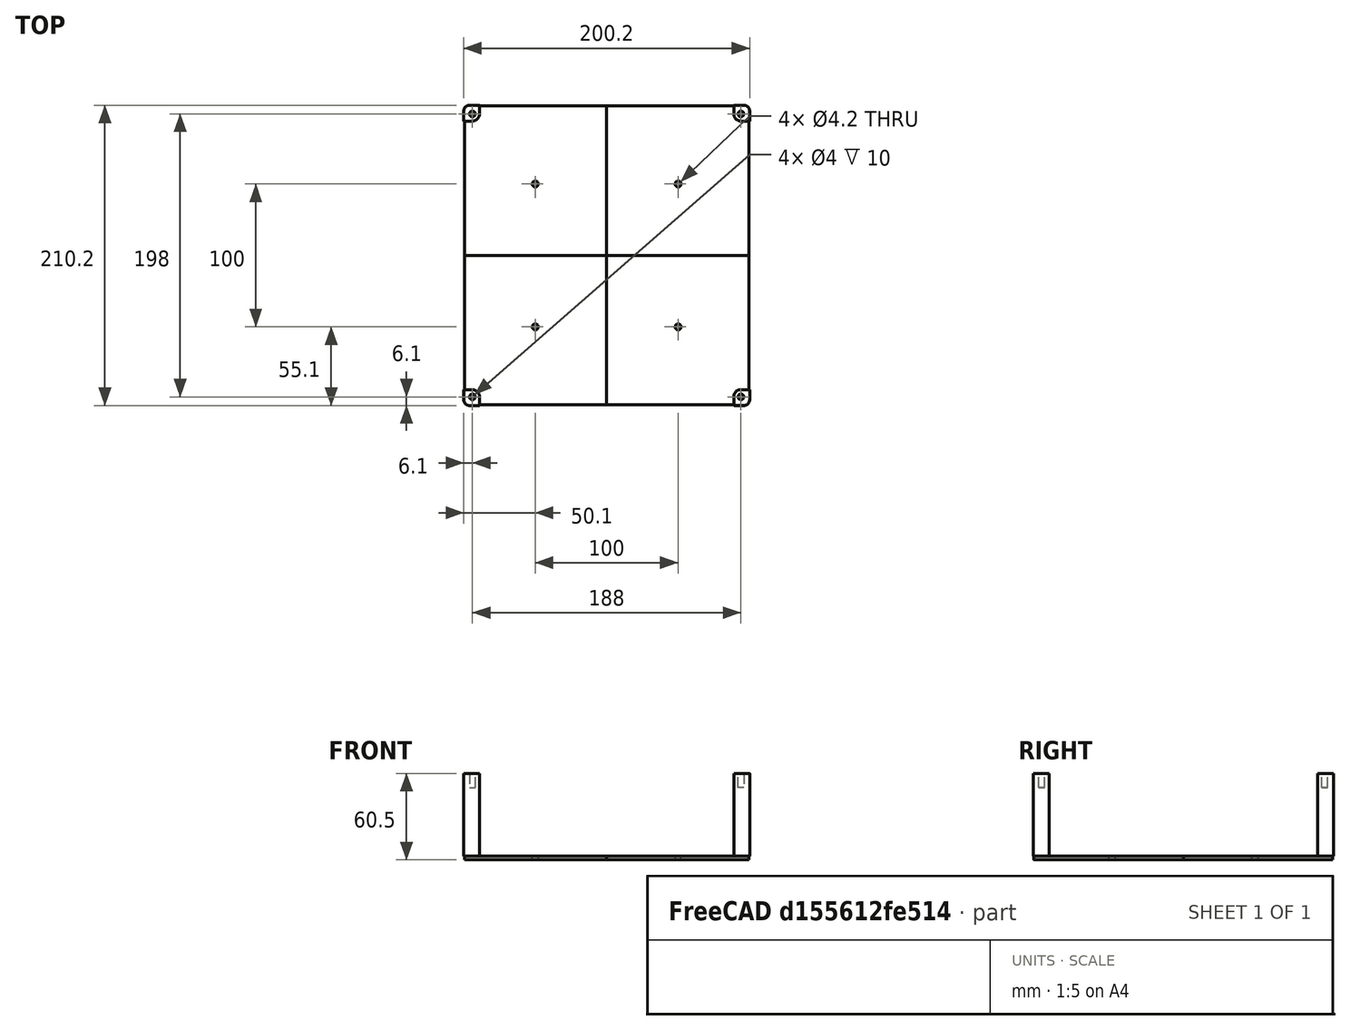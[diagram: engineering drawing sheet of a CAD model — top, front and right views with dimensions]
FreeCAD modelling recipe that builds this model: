
FCSTD DOCUMENT  (FreeCAD 0.20R27078 (Git))
Label: 200x210_back_box#3
License: All rights reserved
LicenseURL: http://en.wikipedia.org/wiki/All_rights_reserved
objects: Sketcher::SketchObject×6, Part::Extrusion×4, Part::Mirroring×3, Part::Cut×2, Part::Compound×2, Spreadsheet::Sheet×1, Part::Sweep×1, Part::Plane×1, Part::Fillet×1, Mesh::Feature×1
note: 20 computed .brp shape members not serialized (recipe doc carries the construction recipe); baked Part::Feature solids carry a one-line shape summary decoded from their .brp

FEATURE [Spreadsheet::Sheet] Spreadsheet
  cells = A1=panel_edge_x; B1(panel_edge_x)=200; A2=panel_edge_y; B2(panel_edge_y)=210; A3=panel_edge_clearance; B3(panel_edge_clearance)=0.1; A4=panel_mount_x; B4(panel_mount_x)=188; A5=panel_mount_y; B5(panel_mount_y)=198; A6=panel_mount_dia; B6(panel_mount_dia)=3.2; A7=panel_corner_radius; B7(panel_corner_radius)=4; A8=panel_thickness; B8(panel_thickness)=2.5; A9=panel_boss_dia; B9(panel_boss_dia)=10; A10=panel_screw_minor_dia; B10(panel_screw_minor_dia)=4; A11=side_internal_height; B11(side_internal_height)=60; A12=side_radius; B12(side_radius)=3; A13=side_radius_internal_offset; B13(side_radius_internal_offset)=0.5; A14=side_thickness; B14(side_thickness)=2.5; A15=back_mount_x; B15(back_mount_x)=100; A16=back_mount_y; B16(back_mount_y)=100; A17=back_mount_dia; B17(back_mount_dia)=4.2; A18=back_thickness; B18(back_thickness)=2.5; A19=cable_entry_z; B19(cable_entry_z)=30; A20=cable_entry_y; B20(cable_entry_y)=40; A21=cable_entry_dia; B21(cable_entry_dia)=10
FEATURE [Sketcher::SketchObject] Sketch  label="Panel layout sketch"
  FullyConstrained = true
  expr: Constraints[14] = Spreadsheet.panel_corner_radius
  expr: Constraints[15] = Spreadsheet.panel_mount_dia
  expr: Constraints[16] = Spreadsheet.panel_mount_x / 2
  expr: Constraints[17] = Spreadsheet.panel_mount_y / 2
  expr: Constraints[8] = Spreadsheet.panel_edge_x / 2 + Spreadsheet.panel_edge_clearance
  expr: Constraints[9] = Spreadsheet.panel_edge_y / 2 + Spreadsheet.panel_edge_clearance
  sketch-geometry (7):
    g0: LineSegment StartX=0 StartY=0 StartZ=0 EndX=100.1 EndY=0 EndZ=0
    g1: LineSegment StartX=100.1 StartY=0 StartZ=0 EndX=100.1 EndY=101.1 EndZ=0
    g2: LineSegment StartX=96.1 StartY=105.1 StartZ=0 EndX=0 EndY=105.1 EndZ=0
    g3: LineSegment StartX=0 StartY=105.1 StartZ=0 EndX=0 EndY=0 EndZ=0
    g4: ArcOfCircle CenterX=96.1 CenterY=101.1 CenterZ=0 NormalX=0 NormalY=0 NormalZ=1 AngleXU=0 Radius=4 StartAngle=1.2e-15 EndAngle=1.5708
    g5: GeomPoint X=100.1 Y=105.1 Z=0
    g6: Circle CenterX=94 CenterY=99 CenterZ=0 NormalX=0 NormalY=0 NormalZ=1 AngleXU=0 Radius=1.6
  constraints (18):
    c: Coincident(g0,g1)
    c: Coincident(g2,g3)
    c: Coincident(g3,g0)
    c: Horizontal(g0)
    c: Horizontal(g2)
    c: Vertical(g1)
    c: Vertical(g3)
    c: Coincident(g0,g-1)
    c: DistanceX(g2,g5) = 100.1
    c: DistanceY(g1,g5) = 105.1
    c: PointOnObject(g5,g2)
    c: PointOnObject(g5,g1)
    c: Tangent(g2,g4) = -1.5708
    c: Tangent(g1,g4) = -1.5708
    c: Radius(g4) = 4
    c: Diameter(g6) = 3.2
    c: DistanceX(g6) = 94
    c: DistanceY(g6) = 99
FEATURE [Sketcher::SketchObject] Sketch001  label="Side profile sketch"
  FullyConstrained = true
  Placement = pos=(0,1,0) rot=(1,0,0;1.5708rad)
  expr: Constraints[10] = Spreadsheet.side_thickness
  expr: Constraints[14] = Spreadsheet.side_radius
  expr: Constraints[15] = Spreadsheet.panel_edge_x / 2 + Spreadsheet.panel_edge_clearance
  expr: Constraints[16] = Spreadsheet.side_radius
  expr: Constraints[17] = Spreadsheet.side_internal_height
  sketch-geometry (6):
    g0: LineSegment StartX=100.1 StartY=63 StartZ=0 EndX=102.6 EndY=63 EndZ=0
    g1: LineSegment StartX=102.6 StartY=63 StartZ=0 EndX=102.6 EndY=3 EndZ=0
    g2: LineSegment StartX=100.1 StartY=3 StartZ=0 EndX=100.1 EndY=63 EndZ=0
    g3: ArcOfCircle CenterX=99.6 CenterY=3 CenterZ=0 NormalX=0 NormalY=0 NormalZ=1 AngleXU=0 Radius=0.5 StartAngle=4.71239 EndAngle=6.28319
    g4: ArcOfCircle CenterX=99.6 CenterY=3 CenterZ=0 NormalX=0 NormalY=0 NormalZ=1 AngleXU=0 Radius=3 StartAngle=4.71239 EndAngle=6.28319
    g5: LineSegment StartX=99.6 StartY=2.5 StartZ=0 EndX=99.6 EndY=-4e-16 EndZ=0
  constraints (18):
    c: Coincident(g0,g1)
    c: Coincident(g2,g0)
    c: Horizontal(g0)
    c: Vertical(g1)
    c: Vertical(g2)
    c: Coincident(g5,g3)
    c: Coincident(g5,g4)
    c: Vertical(g5)
    c: Tangent(g4,g1) = 1.5708
    c: Tangent(g3,g2) = -1.5708
    c: DistanceX(g0,g0) = 2.5
    c: Perpendicular(g3,g5)
    c: Perpendicular(g4,g5)
    c: Horizontal(g2,g1)
    c: Radius(g4) = 3
    c: DistanceX(g2) = 100.1
    c: DistanceY(g2) = 3
    c: DistanceY(g1,g1) = 60
FEATURE [Part::Sweep] Sweep  label="Side wall"
  Frenet = false
  Sections = -> [Sketch001]
  Solid = false
  Spine = -> Sketch [Edge2,Edge3,Edge4]
  Transition = 1
FEATURE [Sketcher::SketchObject] Sketch002  label="Back layout sketch"
  FullyConstrained = true
  expr: Constraints[12] = Spreadsheet.panel_corner_radius - Spreadsheet.side_radius_internal_offset
  expr: Constraints[13] = Spreadsheet.panel_edge_y / 2 + Spreadsheet.panel_edge_clearance - Spreadsheet.side_radius_internal_offset
  expr: Constraints[14] = Spreadsheet.panel_edge_x / 2 + Spreadsheet.panel_edge_clearance - Spreadsheet.side_radius_internal_offset
  expr: Constraints[15] = Spreadsheet.back_mount_dia
  expr: Constraints[16] = Spreadsheet.back_mount_x / 2
  expr: Constraints[17] = Spreadsheet.back_mount_y / 2
  sketch-geometry (7):
    g0: LineSegment StartX=0 StartY=0 StartZ=0 EndX=99.6 EndY=0 EndZ=0
    g1: LineSegment StartX=99.6 StartY=0 StartZ=0 EndX=99.6 EndY=101.1 EndZ=0
    g2: LineSegment StartX=96.1 StartY=104.6 StartZ=0 EndX=0 EndY=104.6 EndZ=0
    g3: LineSegment StartX=0 StartY=104.6 StartZ=0 EndX=0 EndY=0 EndZ=0
    g4: ArcOfCircle CenterX=96.1 CenterY=101.1 CenterZ=0 NormalX=0 NormalY=0 NormalZ=1 AngleXU=0 Radius=3.5 StartAngle=3e-16 EndAngle=1.5708
    g5: GeomPoint X=99.6 Y=104.6 Z=0
    g6: Circle CenterX=50 CenterY=50 CenterZ=0 NormalX=0 NormalY=0 NormalZ=1 AngleXU=0 Radius=2.1
  constraints (18):
    c: Coincident(g0,g1)
    c: Coincident(g2,g3)
    c: Coincident(g3,g0)
    c: Horizontal(g0)
    c: Horizontal(g2)
    c: Vertical(g1)
    c: Vertical(g3)
    c: Coincident(g0,g-1)
    c: PointOnObject(g5,g2)
    c: PointOnObject(g5,g1)
    c: Tangent(g2,g4) = -1.5708
    c: Tangent(g1,g4) = -1.5708
    c: Radius(g4) = 3.5
    c: DistanceY(g2) = 104.6
    c: DistanceX(g1) = 99.6
    c: Diameter(g6) = 4.2
    c: DistanceX(g6) = 50
    c: DistanceY(g6) = 50
FEATURE [Part::Extrusion] Extrude  label="Back"
  Base = -> Sketch002
  Dir = (0,0,1)
  DirMode = 2
  FaceMakerClass = Part::FaceMakerBullseye
  LengthFwd = 2.5
  LengthRev = 0
  Solid = true
  Symmetric = false
  expr: LengthFwd = Spreadsheet.back_thickness
FEATURE [Sketcher::SketchObject] Sketch003  label="Panel mounting boss sketch"
  FullyConstrained = true
  expr: Constraints[10] = Spreadsheet.panel_mount_x / 2
  expr: Constraints[11] = Spreadsheet.panel_mount_y / 2
  expr: Constraints[12] = Spreadsheet.panel_boss_dia
  expr: Constraints[13] = Spreadsheet.panel_edge_x / 2 + Spreadsheet.panel_edge_clearance
  expr: Constraints[14] = Spreadsheet.panel_edge_y / 2 + Spreadsheet.panel_edge_clearance
  expr: Constraints[15] = Spreadsheet.panel_corner_radius
  sketch-geometry (7):
    g0: LineSegment StartX=94 StartY=94 StartZ=0 EndX=100.1 EndY=94 EndZ=0
    g1: LineSegment StartX=100.1 StartY=94 StartZ=0 EndX=100.1 EndY=101.1 EndZ=0
    g2: LineSegment StartX=96.1 StartY=105.1 StartZ=0 EndX=89 EndY=105.1 EndZ=0
    g3: LineSegment StartX=89 StartY=105.1 StartZ=0 EndX=89 EndY=99 EndZ=0
    g4: ArcOfCircle CenterX=94 CenterY=99 CenterZ=0 NormalX=0 NormalY=0 NormalZ=1 AngleXU=0 Radius=5 StartAngle=3.14159 EndAngle=4.71239
    g5: ArcOfCircle CenterX=96.1 CenterY=101.1 CenterZ=0 NormalX=0 NormalY=0 NormalZ=1 AngleXU=0 Radius=4 StartAngle=5e-16 EndAngle=1.5708
    g6: GeomPoint X=100.1 Y=105.1 Z=0
  constraints (18):
    c: Coincident(g0,g1)
    c: Coincident(g2,g3)
    c: Horizontal(g0)
    c: Horizontal(g2)
    c: Vertical(g1)
    c: Vertical(g3)
    c: PointOnObject(g6,g2)
    c: PointOnObject(g6,g1)
    c: Tangent(g2,g5) = -1.5708
    c: Tangent(g1,g5) = -1.5708
    c: DistanceX(g4) = 94
    c: DistanceY(g4) = 99
    c: Diameter(g4) = 10
    c: DistanceX(g1) = 100.1
    c: DistanceY(g2) = 105.1
    c: Radius(g5) = 4
    c: Tangent(g4,g0) = -1.5708
    c: Tangent(g4,g3) = -1.5708
FEATURE [Part::Extrusion] Extrude001  label="Panel mounting boss"
  Base = -> Sketch003
  Dir = (0,0,1)
  DirMode = 2
  FaceMakerClass = Part::FaceMakerBullseye
  LengthFwd = 58
  LengthRev = 0
  Placement = pos=(0,0,2.5) rot=(0,0,1;0rad)
  Solid = true
  Symmetric = false
  expr: .Placement.Base.z = Spreadsheet.back_thickness
  expr: LengthFwd = Spreadsheet.side_internal_height + Spreadsheet.side_radius_internal_offset - Spreadsheet.panel_thickness
FEATURE [Sketcher::SketchObject] Sketch004  label="Panel mounting hole sketch"
  FullyConstrained = true
  expr: Constraints[0] = Spreadsheet.panel_screw_minor_dia
  expr: Constraints[1] = Spreadsheet.panel_mount_x / 2
  expr: Constraints[2] = Spreadsheet.panel_mount_y / 2
  sketch-geometry (1):
    g0: Circle CenterX=94 CenterY=99 CenterZ=0 NormalX=0 NormalY=0 NormalZ=1 AngleXU=0 Radius=2
  constraints (3):
    c: Diameter(g0) = 4
    c: DistanceX(g0) = 94
    c: DistanceY(g0) = 99
FEATURE [Part::Extrusion] Extrude002  label="Panel mounting hole"
  Base = -> Sketch004
  Dir = (0,0,1)
  DirMode = 2
  FaceMakerClass = Part::FaceMakerBullseye
  LengthFwd = 10
  LengthRev = 0
  Placement = pos=(0,0,60.5) rot=(0,0,1;0rad)
  Reversed = true
  Solid = true
  Symmetric = false
  expr: .Placement.Base.z = Spreadsheet.side_internal_height - Spreadsheet.panel_thickness + Spreadsheet.back_thickness + Spreadsheet.side_radius_internal_offset
  expr: LengthFwd = 10
FEATURE [Part::Cut] Cut  label="Panel mounting"
  Base = -> Extrude001
  Tool = -> Extrude002
FEATURE [Part::Compound] Compound  label="Body quadrant w/o fillet"
  Links = -> [Sweep,Extrude,Cut]
FEATURE [Sketcher::SketchObject] Sketch005  label="Cable entry sketch"
  FullyConstrained = true
  Placement = pos=(0,0,0) rot=(0.57735,0.57735,0.57735;2.0944rad)
  expr: Constraints[0] = Spreadsheet.cable_entry_dia
  expr: Constraints[1] = -Spreadsheet.cable_entry_y
  expr: Constraints[2] = Spreadsheet.cable_entry_z + Spreadsheet.back_thickness
  sketch-geometry (1):
    g0: Circle CenterX=-40 CenterY=32.5 CenterZ=0 NormalX=0 NormalY=0 NormalZ=1 AngleXU=0 Radius=5
  constraints (3):
    c: Diameter(g0) = 10
    c: DistanceX(g0) = -40
    c: DistanceY(g0) = 32.5
FEATURE [Part::Extrusion] Extrude003  label="Cable entry"
  Base = -> Sketch005
  Dir = (1,0,0)
  DirMode = 2
  FaceMakerClass = Part::FaceMakerBullseye
  LengthFwd = 2.5
  LengthRev = 0
  Placement = pos=(100.1,0,0) rot=(0,0,1;0rad)
  Solid = true
  Symmetric = false
  expr: .Placement.Base.x = Spreadsheet.panel_edge_x / 2 + Spreadsheet.panel_edge_clearance
  expr: LengthFwd = Spreadsheet.side_thickness
FEATURE [Part::Plane] Plane
  AttacherType = Attacher::AttachEngine3D
  Length = 250
  Placement = pos=(-125,-125,55) rot=(0,0,1;0rad)
  Width = 250
FEATURE [Part::Fillet] Fillet  label="Body quadrant (Original)"
  Base = -> Compound
  Edges = 1 edges r=1: [Edge3]
FEATURE [Part::Mirroring] Part__Mirroring  label="Body quadrant (Mirror #1)"
  Base = (0,0,0)
  Normal = (1,0,0)
  Source = -> Fillet
FEATURE [Part::Mirroring] Part__Mirroring001  label="Body quadrant (Mirror #2)"
  Base = (0,0,0)
  Normal = (0,1,0)
  Source = -> Part__Mirroring
FEATURE [Part::Mirroring] Part__Mirroring002  label="Body quadrant (Mirror #3)"
  Base = (0,0,0)
  Normal = (1,0,0)
  Source = -> Part__Mirroring001
FEATURE [Part::Compound] Compound001  label="Body"
  Links = -> [Part__Mirroring002,Part__Mirroring001,Part__Mirroring,Fillet]
FEATURE [Part::Cut] Cut001  label="Body with cable entry"
  Base = -> Compound001
  Tool = -> Extrude003
FEATURE [Mesh::Feature] Mesh  label="Body with cable entry (Meshed)"
